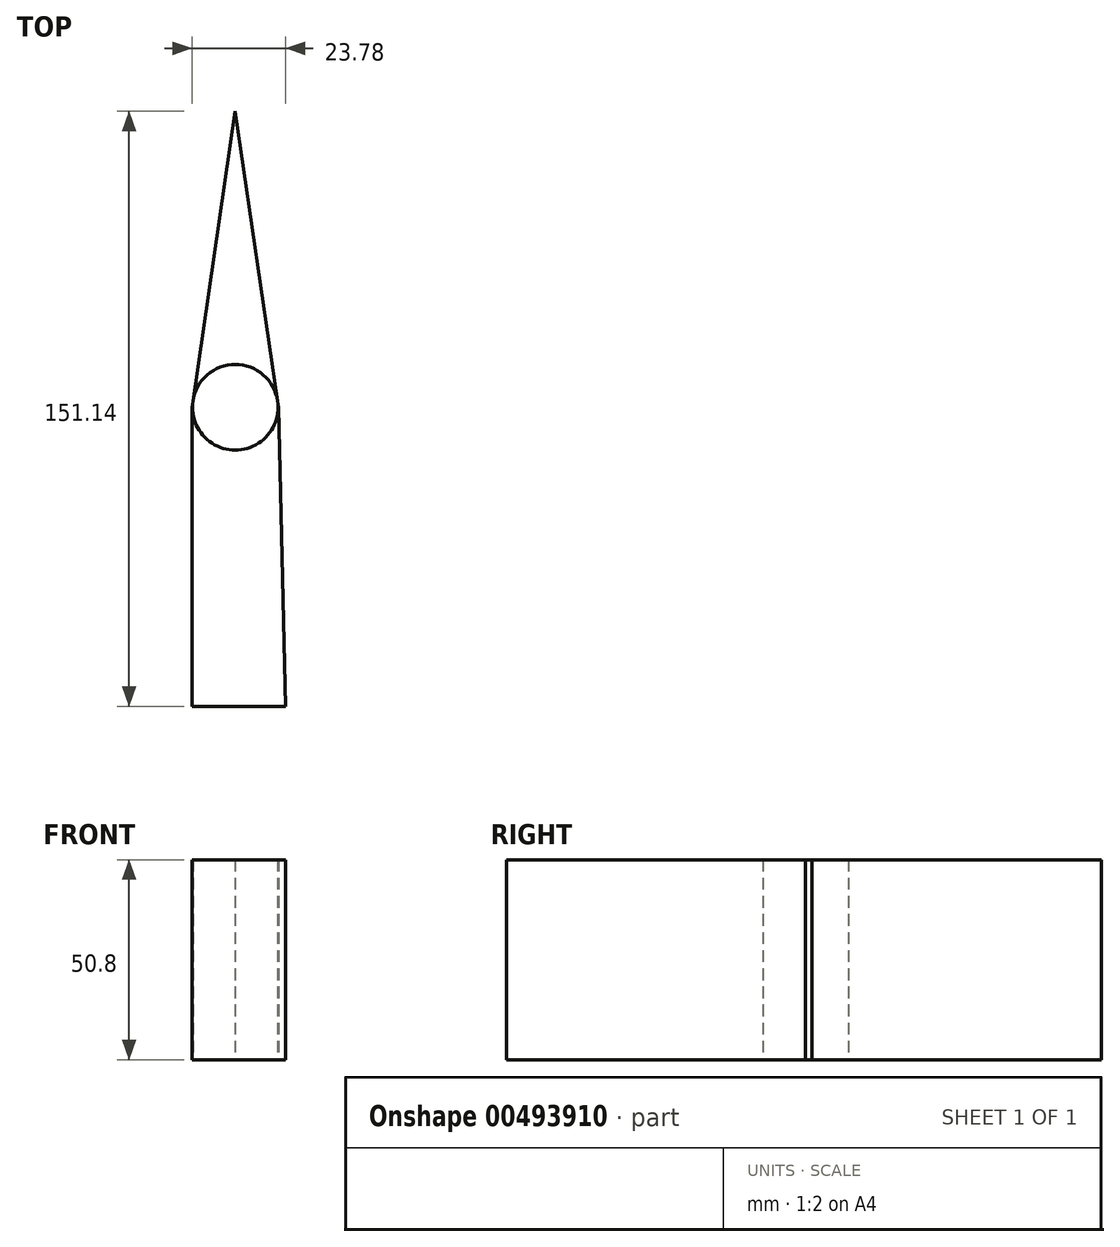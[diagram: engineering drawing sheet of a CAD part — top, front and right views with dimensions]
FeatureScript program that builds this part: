
annotation { "Feature Type Name" : "Feature", "Feature Type Description" : "" }
export const myFeature = defineFeature(function(context is Context, id is Id, definition is map)
    precondition{}
    {
        {
            var Q0;
            Q0=qCreatedBy(makeId("Top.planeOp"),FACE);
            var sketch = newSketch(context, id + "F0", { "sketchPlane" : qUnion([Q0])});
            skLineSegment(sketch, "E0", {"start": v(0, 75.17) * mm, "end": v(0, 0) * mm});
            skLineSegment(sketch, "E1", {"start": v(0, 0) * mm, "end": v(0, -75.97) * mm});
            skCircle(sketch, "E2", {"center": v(0, 0) * mm, "radius": 10.88 * mm});
            skLineSegment(sketch, "E3", {"start": v(0, 75.17) * mm, "end": v(-11, 0) * mm});
            skLineSegment(sketch, "E4", {"start": v(-11, 0) * mm, "end": v(-11, -75.97) * mm});
            skLineSegment(sketch, "E5", {"start": v(-11, -75.97) * mm, "end": v(3.01, -75.97) * mm});
            skLineSegment(sketch, "E6", {"start": v(0, 75.17) * mm, "end": v(11, 0) * mm});
            skLineSegment(sketch, "E7", {"start": v(11, 0) * mm, "end": v(12.79, -75.97) * mm});
            skLineSegment(sketch, "E8", {"start": v(0, -75.97) * mm, "end": v(12.79, -75.97) * mm});
            skSolve(sketch);
        }
        {
            var Q0;
            {var subQ0=sQuery(id+"F0.wireOp",EDGE,"E3");var subQ3=sQuery(id+"F0.wireOp",EDGE,"E2");var subQ5=makeQuery(id+"F0.imprint","INTERSECT",VERTEX,{"derivedFrom":[subQ3,subQ0]});Q0=makeQuery(id+"F0.imprint","IMPRINT",FACE,{"disambiguationData":[TD([[makeQuery(id+"F0.imprint","IMPRINT",EDGE,{"disambiguationData":[TD([[subQ5,1.0]])],"derivedFrom":subQ3}),-1.0]])]});}
            var Q1;
            {var subQ0=sQuery(id+"F0.wireOp",EDGE,"E6");var subQ3=sQuery(id+"F0.wireOp",EDGE,"E2");var subQ5=makeQuery(id+"F0.imprint","INTERSECT",VERTEX,{"derivedFrom":[subQ3,subQ0]});Q1=makeQuery(id+"F0.imprint","IMPRINT",FACE,{"disambiguationData":[TD([[makeQuery(id+"F0.imprint","IMPRINT",EDGE,{"disambiguationData":[TD([[subQ5,-1.0]])],"derivedFrom":subQ3}),-1.0]])]});}
            var Q2;
            {var subQ0=sQuery(id+"F0.wireOp",EDGE,"E7");Q2=makeQuery(id+"F0.imprint","IMPRINT",FACE,{"disambiguationData":[TD([[makeQuery(id+"F0.imprint","IMPRINT",EDGE,{"derivedFrom":subQ0}),-1.0]])]});}
            var Q3;
            {var subQ0=sQuery(id+"F0.wireOp",EDGE,"E4");Q3=makeQuery(id+"F0.imprint","IMPRINT",FACE,{"disambiguationData":[TD([[makeQuery(id+"F0.imprint","IMPRINT",EDGE,{"derivedFrom":subQ0}),1.0]])]});}
            extrude(context, id + "F1", {"entities" : qUnion([Q0, Q1, Q2, Q3]), "depth" : 50.8 * mm});
        }
    });
